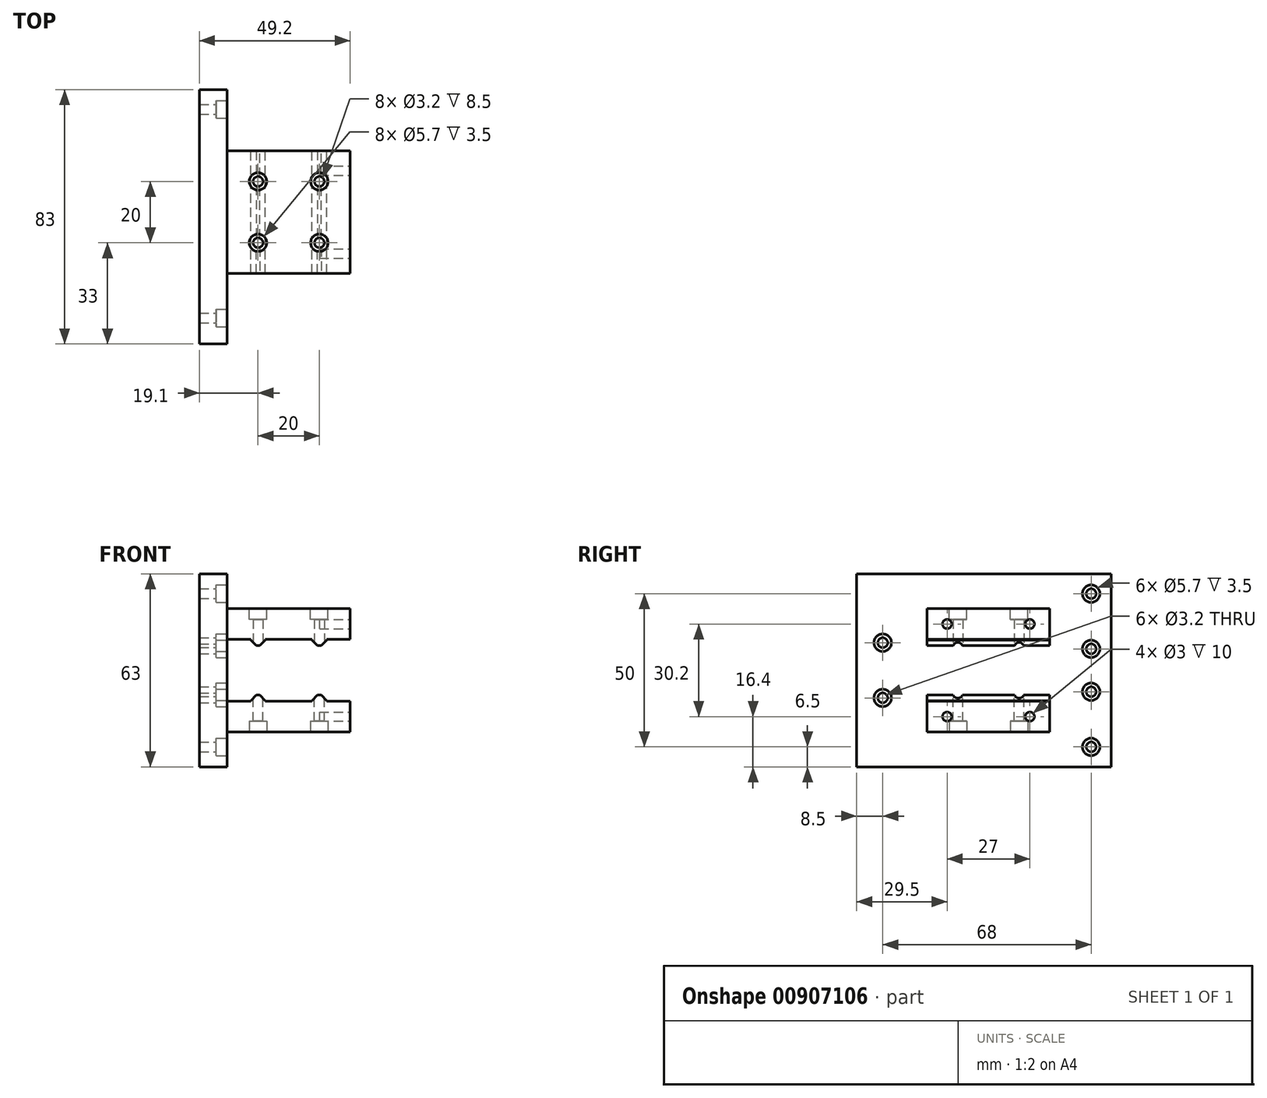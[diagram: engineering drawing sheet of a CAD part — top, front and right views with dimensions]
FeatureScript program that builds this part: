
annotation { "Feature Type Name" : "Feature", "Feature Type Description" : "" }
export const myFeature = defineFeature(function(context is Context, id is Id, definition is map)
    precondition{}
    {
        {
            assignVariable(context, id + "F0", {"name" : "headdepth", "anyValue" : 3.5 * mm});
        }
        {
            var Q0;
            Q0=qCreatedBy(makeId("Top.planeOp"),FACE);
            var sketch = newSketch(context, id + "F1", { "sketchPlane" : qUnion([Q0])});
            skLineSegment(sketch, "E0.bottom", {"start": v(0, 0) * mm, "end": v(9, 0) * mm});
            skLineSegment(sketch, "E0.top", {"start": v(0, 83) * mm, "end": v(9, 83) * mm});
            skLineSegment(sketch, "E0.left", {"start": v(0, 0) * mm, "end": v(0, 83) * mm});
            skLineSegment(sketch, "E0.right", {"start": v(9, 0) * mm, "end": v(9, 83) * mm});
            skSolve(sketch);
        }
        {
            var Q0;
            Q0=qSketchRegion(id+"F1",true);
            var Q1;
            Q1=makeQuery(id+"F1.imprint","IMPRINT",FACE,{"disambiguationData":[TD([[makeQuery(id+"F1.imprint","IMPRINT",EDGE,{"derivedFrom":sQuery(id+"F1.wireOp",EDGE,"E0.bottom")}),1.0]])]});
            extrude(context, id + "F2", {"entities" : qUnion([Q0, Q1]), "depth" : 63 * mm, "offsetDistance" : 25 * mm});
        }
        {
            var Q0;
            Q0=makeQuery(id+"F2.opExtrude","SWEPT_FACE",FACE,{"disambiguationData":[OSD([sQuery(id+"F1.wireOp",EDGE,"E0.right")])]});
            var sketch = newSketch(context, id + "F3", { "sketchPlane" : qUnion([Q0])});
            skLineSegment(sketch, "E1", {"start": v(83, 6.5) * mm, "end": v(0, 6.5) * mm, "construction": true});
            skLineSegment(sketch, "E2", {"start": v(0, 24.5) * mm, "end": v(83, 24.5) * mm, "construction": true});
            skLineSegment(sketch, "E3", {"start": v(83, 38.5) * mm, "end": v(0, 38.5) * mm, "construction": true});
            skLineSegment(sketch, "E4", {"start": v(0, 56.5) * mm, "end": v(83, 56.5) * mm, "construction": true});
            skLineSegment(sketch, "E5", {"start": v(76.5, 63) * mm, "end": v(76.5, 0) * mm, "construction": true});
            skLineSegment(sketch, "E6", {"start": v(8.5, 63) * mm, "end": v(8.5, 0) * mm, "construction": true});
            skLineSegment(sketch, "E7", {"start": v(0, 22.5) * mm, "end": v(8.5, 22.5) * mm, "construction": true});
            skLineSegment(sketch, "E8", {"start": v(0, 40.5) * mm, "end": v(8.5, 40.5) * mm, "construction": true});
            skCircle(sketch, "E9", {"center": v(8.5, 40.5) * mm, "radius": 2.85 * mm});
            skCircle(sketch, "E10", {"center": v(8.5, 22.5) * mm, "radius": 2.85 * mm});
            skCircle(sketch, "E11", {"center": v(76.5, 56.5) * mm, "radius": 2.85 * mm});
            skCircle(sketch, "E12", {"center": v(76.5, 38.5) * mm, "radius": 2.85 * mm});
            skCircle(sketch, "E13", {"center": v(76.5, 24.5) * mm, "radius": 2.85 * mm});
            skCircle(sketch, "E14", {"center": v(76.5, 6.5) * mm, "radius": 2.85 * mm});
            skSolve(sketch);
        }
        {
            var Q0;
            Q0=qSketchRegion(id+"F3",true);
            var Q1;
            Q1=makeQuery(id+"F3.imprint","IMPRINT",FACE,{"disambiguationData":[TD([[makeQuery(id+"F3.imprint","IMPRINT",EDGE,{"derivedFrom":sQuery(id+"F3.wireOp",EDGE,"E9")}),1.0]])]});
            extrude(context, id + "F4", {"entities" : qUnion([Q0, Q1]), "operationType" : NewBodyOperationType.REMOVE, "oppositeDirection" : true, "depth" : getVariable(context, 'headdepth'), "offsetDistance" : 25 * mm});
        }
        {
            var Q0;
            Q0=makeQuery(id+"F3.imprint","IMPRINT",FACE,{"disambiguationData":[TD([[makeQuery(id+"F3.imprint","IMPRINT",EDGE,{"derivedFrom":sQuery(id+"F3.wireOp",EDGE,"E9")}),1.0]])]});
            var sketch = newSketch(context, id + "F5", { "sketchPlane" : qUnion([Q0])});
            skCircle(sketch, "E15", {"center": v(8.5, 40.5) * mm, "radius": 1.6 * mm});
            skCircle(sketch, "E16", {"center": v(8.5, 22.5) * mm, "radius": 1.6 * mm});
            skCircle(sketch, "E17", {"center": v(76.5, 24.5) * mm, "radius": 1.6 * mm});
            skCircle(sketch, "E18", {"center": v(76.5, 38.5) * mm, "radius": 1.6 * mm});
            skCircle(sketch, "E19", {"center": v(76.5, 56.5) * mm, "radius": 1.6 * mm});
            skCircle(sketch, "E20", {"center": v(76.5, 6.5) * mm, "radius": 1.6 * mm});
            skSolve(sketch);
        }
        {
            var Q0;
            Q0=qSketchRegion(id+"F5",true);
            extrude(context, id + "F6", {"entities" : qUnion([Q0]), "operationType" : NewBodyOperationType.REMOVE, "oppositeDirection" : true, "depth" : 25 * mm, "offsetDistance" : 25 * mm});
        }
        {
            var Q0;
            Q0=makeQuery(id+"F2.opExtrude","SWEPT_FACE",FACE,{"disambiguationData":[OSD([sQuery(id+"F1.wireOp",EDGE,"E0.right")])]});
            var sketch = newSketch(context, id + "F7", { "sketchPlane" : qUnion([Q0])});
            skLineSegment(sketch, "E21", {"start": v(83, 31.5) * mm, "end": v(0, 31.5) * mm, "construction": true});
            skLineSegment(sketch, "E22.bottom", {"start": v(63, 41.6) * mm, "end": v(23, 41.6) * mm});
            skLineSegment(sketch, "E22.top", {"start": v(63, 51.6) * mm, "end": v(23, 51.6) * mm});
            skLineSegment(sketch, "E22.left", {"start": v(63, 41.6) * mm, "end": v(63, 51.6) * mm});
            skLineSegment(sketch, "E22.right", {"start": v(23, 41.6) * mm, "end": v(23, 51.6) * mm});
            skLineSegment(sketch, "E23.MirrorCS", {"start": v(63, 21.4) * mm, "end": v(63, 11.4) * mm});
            skLineSegment(sketch, "E24.MirrorCS", {"start": v(63, 21.4) * mm, "end": v(23, 21.4) * mm});
            skLineSegment(sketch, "E25.MirrorCS", {"start": v(63, 11.4) * mm, "end": v(23, 11.4) * mm});
            skLineSegment(sketch, "E26.MirrorCS", {"start": v(23, 21.4) * mm, "end": v(23, 11.4) * mm});
            skSolve(sketch);
        }
        {
            var Q0;
            Q0=makeQuery(id+"F7.imprint","IMPRINT",FACE,{"disambiguationData":[TD([[makeQuery(id+"F7.imprint","IMPRINT",EDGE,{"derivedFrom":sQuery(id+"F7.wireOp",EDGE,"E23.MirrorCS")}),-1.0]])]});
            var Q1;
            Q1=makeQuery(id+"F7.imprint","IMPRINT",FACE,{"disambiguationData":[TD([[makeQuery(id+"F7.imprint","IMPRINT",EDGE,{"derivedFrom":sQuery(id+"F7.wireOp",EDGE,"E22.bottom")}),-1.0]])]});
            extrude(context, id + "F8", {"entities" : qUnion([Q0, Q1]), "operationType" : NewBodyOperationType.ADD, "depth" : 40.2 * mm, "offsetDistance" : 25 * mm});
        }
        {
            var Q0;
            Q0=makeQuery(id+"F8.opExtrude","SWEPT_FACE",FACE,{"disambiguationData":[OSD([sQuery(id+"F7.wireOp",EDGE,"E22.bottom")])]});
            var sketch = newSketch(context, id + "F9", { "sketchPlane" : qUnion([Q0])});
            skLineSegment(sketch, "E27", {"start": v(19.1, -23) * mm, "end": v(19.1, -63) * mm, "construction": true});
            skLineSegment(sketch, "E28.bottom", {"start": v(21.5, -23) * mm, "end": v(16.7, -23) * mm});
            skLineSegment(sketch, "E28.top", {"start": v(21.5, -63) * mm, "end": v(16.7, -63) * mm});
            skLineSegment(sketch, "E28.left", {"start": v(21.5, -23) * mm, "end": v(21.5, -63) * mm});
            skLineSegment(sketch, "E28.right", {"start": v(16.7, -23) * mm, "end": v(16.7, -63) * mm});
            skLineSegment(sketch, "E29", {"start": v(29.1, -23) * mm, "end": v(29.1, -63) * mm, "construction": true});
            skLineSegment(sketch, "E30.MirrorCS", {"start": v(36.7, -23) * mm, "end": v(36.7, -63) * mm});
            skLineSegment(sketch, "E31.MirrorCS", {"start": v(41.5, -23) * mm, "end": v(41.5, -63) * mm});
            skLineSegment(sketch, "E32.MirrorCS", {"start": v(36.7, -23) * mm, "end": v(41.5, -23) * mm});
            skLineSegment(sketch, "E33.MirrorCS", {"start": v(36.7, -63) * mm, "end": v(41.5, -63) * mm});
            skSolve(sketch);
        }
        {
            var Q0;
            Q0=qSketchRegion(id+"F9",true);
            extrude(context, id + "F10", {"entities" : qUnion([Q0]), "operationType" : NewBodyOperationType.ADD, "depth" : 2 * mm, "offsetDistance" : 25 * mm});
        }
        {
            var Q0;
            Q0=makeQuery(id+"F10.opExtrude","CAP_EDGE",EDGE,{"disambiguationData":[OSD([sQuery(id+"F9.wireOp",EDGE,"E28.left")])],"isStart":false});
            var Q1;
            Q1=makeQuery(id+"F10.opExtrude","CAP_EDGE",EDGE,{"disambiguationData":[OSD([sQuery(id+"F9.wireOp",EDGE,"E28.right")])],"isStart":false});
            var Q2;
            Q2=makeQuery(id+"F10.opExtrude","CAP_EDGE",EDGE,{"disambiguationData":[OSD([sQuery(id+"F9.wireOp",EDGE,"E31.MirrorCS")])],"isStart":false});
            var Q3;
            Q3=makeQuery(id+"F10.opExtrude","CAP_EDGE",EDGE,{"disambiguationData":[OSD([sQuery(id+"F9.wireOp",EDGE,"E30.MirrorCS")])],"isStart":false});
            chamfer(context, id + "F11", {"entities" : qUnion([Q0, Q1, Q2, Q3]), "width" : 1.8 * mm, "tangentPropagation" : true});
        }
        {
            var Q0;
            Q0=makeQuery(id+"F10.opExtrude","CAP_FACE",FACE,{"disambiguationData":[OSD([sQuery(id+"F9.wireOp",EDGE,"E28.bottom"),sQuery(id+"F9.wireOp",EDGE,"E28.top"),sQuery(id+"F9.wireOp",EDGE,"E28.left"),sQuery(id+"F9.wireOp",EDGE,"E28.right")])],"isStart":false});
            var sketch = newSketch(context, id + "F12", { "sketchPlane" : qUnion([Q0])});
            skLineSegment(sketch, "E34", {"start": v(19.1, -23) * mm, "end": v(19.1, -63) * mm, "construction": true});
            skCircle(sketch, "E35", {"center": v(19.1, -33) * mm, "radius": 1.6 * mm});
            skCircle(sketch, "E36", {"center": v(19.1, -53) * mm, "radius": 1.6 * mm});
            skCircle(sketch, "E37.MirrorC", {"center": v(39.1, -33) * mm, "radius": 1.6 * mm});
            skCircle(sketch, "E38.MirrorC", {"center": v(39.1, -53) * mm, "radius": 1.6 * mm});
            skSolve(sketch);
        }
        {
            var Q0;
            Q0=qSketchRegion(id+"F12",true);
            extrude(context, id + "F13", {"entities" : qUnion([Q0]), "operationType" : NewBodyOperationType.REMOVE, "oppositeDirection" : true, "depth" : 25 * mm, "offsetDistance" : 25 * mm});
        }
        {
            var Q0;
            Q0=makeQuery(id+"F8.opExtrude","SWEPT_FACE",FACE,{"disambiguationData":[OSD([sQuery(id+"F7.wireOp",EDGE,"E24.MirrorCS")])]});
            var sketch = newSketch(context, id + "F14", { "sketchPlane" : qUnion([Q0])});
            skLineSegment(sketch, "E39", {"start": v(19.1, 63) * mm, "end": v(19.1, 23) * mm, "construction": true});
            skLineSegment(sketch, "E40.bottom", {"start": v(21.5, 23) * mm, "end": v(16.7, 23) * mm});
            skLineSegment(sketch, "E40.top", {"start": v(21.5, 63) * mm, "end": v(16.7, 63) * mm});
            skLineSegment(sketch, "E40.left", {"start": v(21.5, 23) * mm, "end": v(21.5, 63) * mm});
            skLineSegment(sketch, "E40.right", {"start": v(16.7, 23) * mm, "end": v(16.7, 63) * mm});
            skLineSegment(sketch, "E41", {"start": v(29.1, 63) * mm, "end": v(29.1, 23) * mm, "construction": true});
            skLineSegment(sketch, "E42.MirrorCS", {"start": v(36.7, 23) * mm, "end": v(36.7, 63) * mm});
            skLineSegment(sketch, "E43.MirrorCS", {"start": v(36.7, 63) * mm, "end": v(41.5, 63) * mm});
            skLineSegment(sketch, "E44.MirrorCS", {"start": v(36.7, 23) * mm, "end": v(41.5, 23) * mm});
            skLineSegment(sketch, "E45.MirrorCS", {"start": v(41.5, 23) * mm, "end": v(41.5, 63) * mm});
            skLineSegment(sketch, "E46", {"start": v(39.1, 63) * mm, "end": v(39.1, 23) * mm, "construction": true});
            skSolve(sketch);
        }
        {
            var Q0;
            Q0=qSketchRegion(id+"F14",true);
            extrude(context, id + "F15", {"entities" : qUnion([Q0]), "operationType" : NewBodyOperationType.ADD, "depth" : 2 * mm, "offsetDistance" : 25 * mm});
        }
        {
            var Q0;
            Q0=makeQuery(id+"F15.opExtrude","CAP_EDGE",EDGE,{"disambiguationData":[OSD([sQuery(id+"F14.wireOp",EDGE,"E40.left")])],"isStart":false});
            var Q1;
            Q1=makeQuery(id+"F15.opExtrude","CAP_EDGE",EDGE,{"disambiguationData":[OSD([sQuery(id+"F14.wireOp",EDGE,"E40.right")])],"isStart":false});
            var Q2;
            Q2=makeQuery(id+"F15.opExtrude","CAP_EDGE",EDGE,{"disambiguationData":[OSD([sQuery(id+"F14.wireOp",EDGE,"E42.MirrorCS")])],"isStart":false});
            var Q3;
            Q3=makeQuery(id+"F15.opExtrude","CAP_EDGE",EDGE,{"disambiguationData":[OSD([sQuery(id+"F14.wireOp",EDGE,"E45.MirrorCS")])],"isStart":false});
            chamfer(context, id + "F16", {"entities" : qUnion([Q0, Q1, Q2, Q3]), "width" : 1.8 * mm, "tangentPropagation" : true});
        }
        {
            var Q0;
            Q0=makeQuery(id+"F15.opExtrude","CAP_FACE",FACE,{"disambiguationData":[OSD([sQuery(id+"F14.wireOp",EDGE,"E40.bottom"),sQuery(id+"F14.wireOp",EDGE,"E40.top"),sQuery(id+"F14.wireOp",EDGE,"E40.left"),sQuery(id+"F14.wireOp",EDGE,"E40.right")])],"isStart":false});
            var sketch = newSketch(context, id + "F17", { "sketchPlane" : qUnion([Q0])});
            skLineSegment(sketch, "E47", {"start": v(19.1, 63) * mm, "end": v(19.1, 23) * mm, "construction": true});
            skCircle(sketch, "E48", {"center": v(19.1, 33) * mm, "radius": 1.6 * mm});
            skCircle(sketch, "E49", {"center": v(19.1, 53) * mm, "radius": 1.6 * mm});
            skCircle(sketch, "E50.MirrorC", {"center": v(39.1, 33) * mm, "radius": 1.6 * mm});
            skCircle(sketch, "E51.MirrorC", {"center": v(39.1, 53) * mm, "radius": 1.6 * mm});
            skSolve(sketch);
        }
        {
            var Q0;
            Q0=qSketchRegion(id+"F17",true);
            extrude(context, id + "F18", {"entities" : qUnion([Q0]), "operationType" : NewBodyOperationType.REMOVE, "oppositeDirection" : true, "depth" : 25 * mm, "offsetDistance" : 25 * mm});
        }
        {
            var Q0;
            Q0=makeQuery(id+"F8.opExtrude","SWEPT_FACE",FACE,{"disambiguationData":[OSD([sQuery(id+"F7.wireOp",EDGE,"E25.MirrorCS")])]});
            var sketch = newSketch(context, id + "F19", { "sketchPlane" : qUnion([Q0])});
            skCircle(sketch, "E52", {"center": v(19.1, -33) * mm, "radius": 2.85 * mm});
            skCircle(sketch, "E53", {"center": v(19.1, -53) * mm, "radius": 2.85 * mm});
            skCircle(sketch, "E54.MirrorC", {"center": v(39.1, -33) * mm, "radius": 2.85 * mm});
            skCircle(sketch, "E55.MirrorC", {"center": v(39.1, -53) * mm, "radius": 2.85 * mm});
            skSolve(sketch);
        }
        {
            var Q0;
            Q0=qSketchRegion(id+"F19",true);
            extrude(context, id + "F20", {"entities" : qUnion([Q0]), "operationType" : NewBodyOperationType.REMOVE, "oppositeDirection" : true, "depth" : 3.5 * mm, "offsetDistance" : 25 * mm});
        }
        {
            var Q0;
            Q0=makeQuery(id+"F8.opExtrude","SWEPT_FACE",FACE,{"disambiguationData":[OSD([sQuery(id+"F7.wireOp",EDGE,"E22.top")])]});
            var sketch = newSketch(context, id + "F21", { "sketchPlane" : qUnion([Q0])});
            skCircle(sketch, "E56", {"center": v(19.1, 53) * mm, "radius": 2.85 * mm});
            skCircle(sketch, "E57", {"center": v(19.1, 33) * mm, "radius": 2.85 * mm});
            skCircle(sketch, "E58.MirrorC", {"center": v(39.1, 53) * mm, "radius": 2.85 * mm});
            skCircle(sketch, "E59.MirrorC", {"center": v(39.1, 33) * mm, "radius": 2.85 * mm});
            skSolve(sketch);
        }
        {
            var Q0;
            Q0=qSketchRegion(id+"F21",true);
            extrude(context, id + "F22", {"entities" : qUnion([Q0]), "operationType" : NewBodyOperationType.REMOVE, "oppositeDirection" : true, "depth" : 3.5 * mm, "offsetDistance" : 25 * mm});
        }
        {
            var Q0;
            Q0=makeQuery(id+"F8.opExtrude","CAP_FACE",FACE,{"disambiguationData":[OSD([sQuery(id+"F7.wireOp",EDGE,"E23.MirrorCS"),sQuery(id+"F7.wireOp",EDGE,"E24.MirrorCS"),sQuery(id+"F7.wireOp",EDGE,"E25.MirrorCS"),sQuery(id+"F7.wireOp",EDGE,"E26.MirrorCS")])],"isStart":false});
            var sketch = newSketch(context, id + "F23", { "sketchPlane" : qUnion([Q0])});
            skLineSegment(sketch, "E60", {"start": v(63, 16.4) * mm, "end": v(23, 16.4) * mm, "construction": true});
            skLineSegment(sketch, "E61", {"start": v(56.5, 11.4) * mm, "end": v(56.5, 21.4) * mm, "construction": true});
            skLineSegment(sketch, "E62", {"start": v(43, 11.4) * mm, "end": v(43, 21.4) * mm, "construction": true});
            skLineSegment(sketch, "E63", {"start": v(29.5, 11.4) * mm, "end": v(29.5, 21.4) * mm, "construction": true});
            skCircle(sketch, "E64", {"center": v(56.5, 16.4) * mm, "radius": 1.5 * mm});
            skCircle(sketch, "E65", {"center": v(29.5, 16.4) * mm, "radius": 1.5 * mm});
            skCircle(sketch, "E66.MirrorC", {"center": v(29.5, 46.6) * mm, "radius": 1.5 * mm});
            skCircle(sketch, "E67.MirrorC", {"center": v(56.5, 46.6) * mm, "radius": 1.5 * mm});
            skSolve(sketch);
        }
        {
            var Q0;
            Q0=qSketchRegion(id+"F23",true);
            extrude(context, id + "F24", {"entities" : qUnion([Q0]), "operationType" : NewBodyOperationType.REMOVE, "oppositeDirection" : true, "depth" : 10 * mm, "offsetDistance" : 25 * mm});
        }
    });
